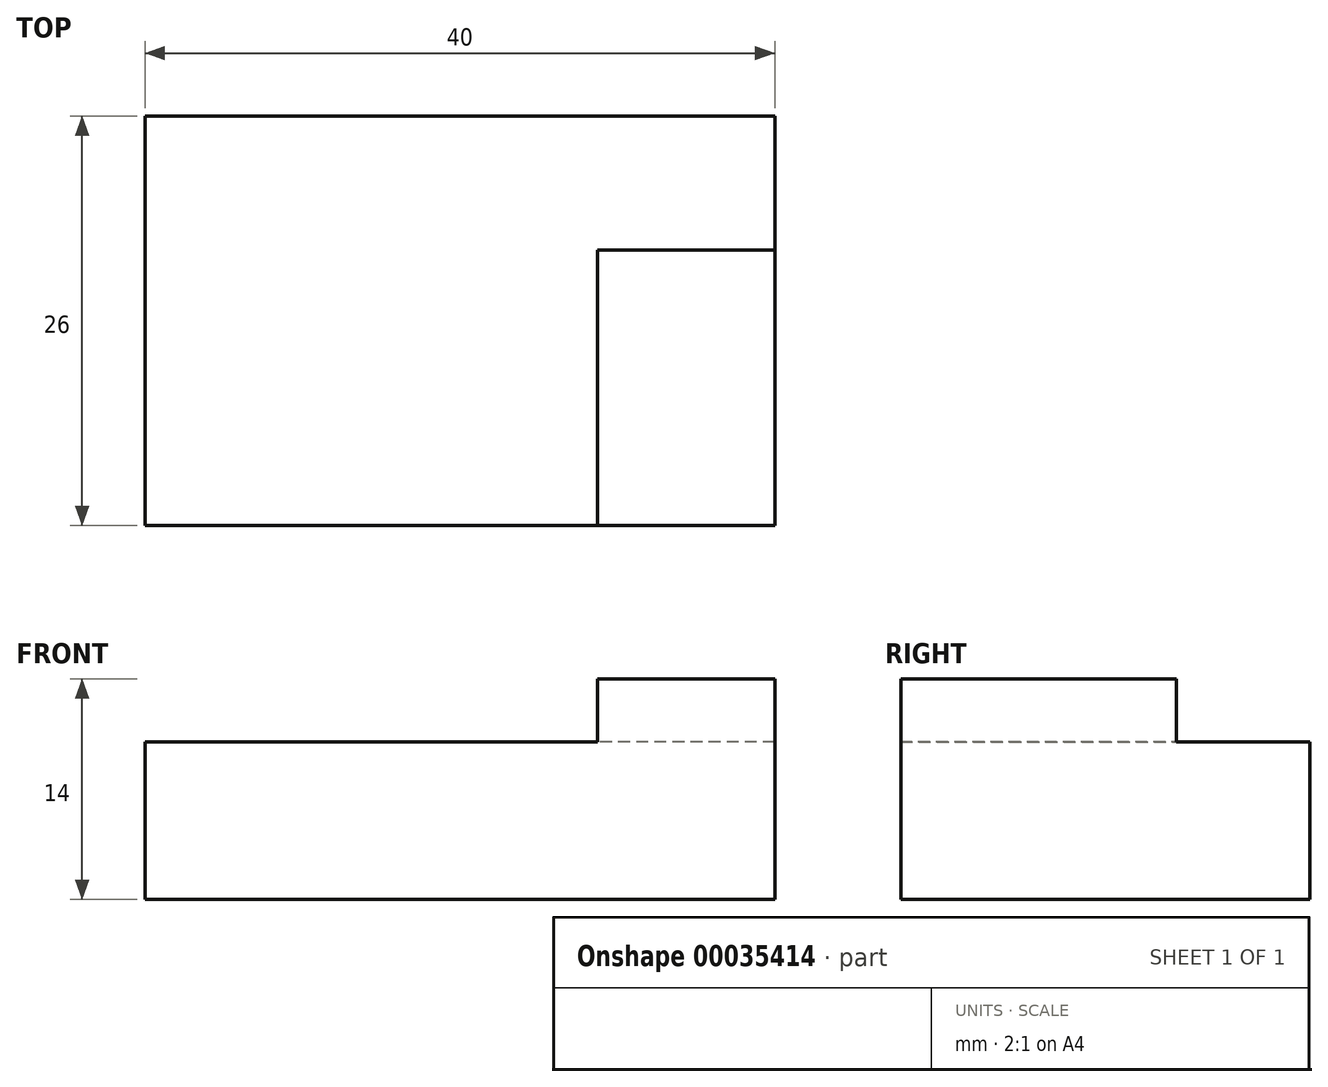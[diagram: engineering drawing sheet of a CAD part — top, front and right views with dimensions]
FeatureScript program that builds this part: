
annotation { "Feature Type Name" : "Feature", "Feature Type Description" : "" }
export const myFeature = defineFeature(function(context is Context, id is Id, definition is map)
    precondition{}
    {
        {
            var Q0;
            Q0=qCreatedBy(makeId("Top.planeOp"),FACE);
            var sketch = newSketch(context, id + "F0", { "sketchPlane" : qUnion([Q0])});
            skLineSegment(sketch, "E0.rect.bottom", {"start": v(-20, 13) * mm, "end": v(20, 13) * mm});
            skLineSegment(sketch, "E0.rect.top", {"start": v(-20, -13) * mm, "end": v(20, -13) * mm});
            skLineSegment(sketch, "E0.rect.left", {"start": v(-20, 13) * mm, "end": v(-20, -13) * mm});
            skLineSegment(sketch, "E0.rect.right", {"start": v(20, 13) * mm, "end": v(20, -13) * mm});
            skPoint(sketch, "E0.rect.middle", {"position": v(0, 0) * mm});
            skSolve(sketch);
        }
        {
            var Q0;
            Q0 = qSketchRegion(id + "F0", true);
            extrude(context, id + "F1", {"entities" : qUnion([Q0]), "depth" : 10 * mm});
        }
        {
            var Q0;
            Q0=makeQuery(id+"F1.opExtrude","CAP_FACE",FACE,{"disambiguationData":[OSD([sQuery(id+"F0.wireOp",EDGE,"E0.rect.bottom"),sQuery(id+"F0.wireOp",EDGE,"E0.rect.top"),sQuery(id+"F0.wireOp",EDGE,"E0.rect.left"),sQuery(id+"F0.wireOp",EDGE,"E0.rect.right")])],"isStart":false});
            var sketch = newSketch(context, id + "F2", { "sketchPlane" : qUnion([Q0])});
            skLineSegment(sketch, "E1.bottom", {"start": v(20, -13) * mm, "end": v(8.75, -13) * mm});
            skLineSegment(sketch, "E1.top", {"start": v(20, 4.5) * mm, "end": v(8.75, 4.5) * mm});
            skLineSegment(sketch, "E1.left", {"start": v(20, -13) * mm, "end": v(20, 4.5) * mm});
            skLineSegment(sketch, "E1.right", {"start": v(8.75, -13) * mm, "end": v(8.75, 4.5) * mm});
            skSolve(sketch);
        }
        {
            var Q0;
            Q0=makeQuery(id+"F2.imprint","IMPRINT",FACE,{"disambiguationData":[TD([[makeQuery(id+"F2.imprint","IMPRINT",EDGE,{"derivedFrom":sQuery(id+"F2.wireOp",EDGE,"E1.bottom")}),1.0]])]});
            extrude(context, id + "F3", {"entities" : qUnion([Q0]), "operationType" : NewBodyOperationType.ADD, "depth" : 4 * mm});
        }
    });
